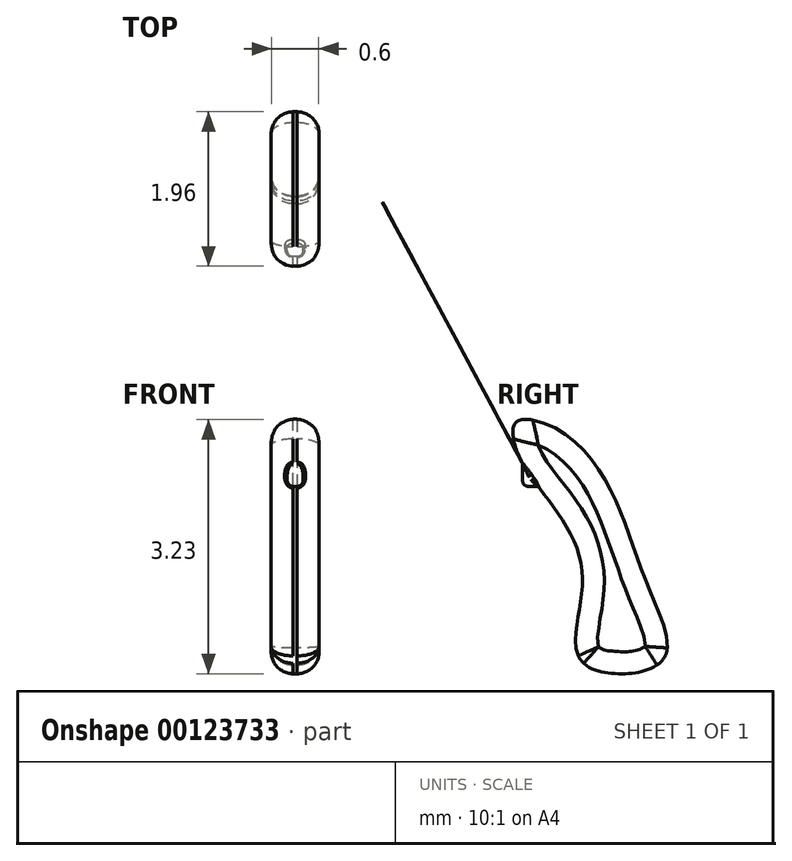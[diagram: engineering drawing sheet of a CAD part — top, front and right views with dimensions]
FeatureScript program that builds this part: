
annotation { "Feature Type Name" : "Feature", "Feature Type Description" : "" }
export const myFeature = defineFeature(function(context is Context, id is Id, definition is map)
    precondition{}
    {
        {
            var Q0;
            Q0=qCreatedBy(makeId("Right.planeOp"),FACE);
            var sketch = newSketch(context, id + "F0", { "sketchPlane" : qUnion([Q0])});
            skFitSpline(sketch, "E0", {"points": [v(0, 0) * mm, v(1, 0) * mm, v(0.83, 0.97) * mm, v(0, 2.7) * mm, v(-0.83, 3.06) * mm, v(-0.84, 2.71) * mm, v(-0.54, 2.2) * mm, v(0, 1.1) * mm, v(0, 0) * mm]});
            skSolve(sketch);
        }
        {
            var Q0;
            Q0=makeQuery(id+"F0.imprint","IMPRINT",FACE,{"disambiguationData":[TD([[makeQuery(id+"F0.imprint","IMPRINT",EDGE,{"derivedFrom":sQuery(id+"F0.wireOp",EDGE,"E0")}),1.0]])]});
            extrude(context, id + "F1", {"entities" : qUnion([Q0]), "depth" : 0.3 * mm});
        }
        {
            var Q0;
            Q0=makeQuery(id+"F0.imprint","IMPRINT",FACE,{"disambiguationData":[TD([[makeQuery(id+"F0.imprint","IMPRINT",EDGE,{"derivedFrom":sQuery(id+"F0.wireOp",EDGE,"E0")}),1.0]])]});
            extrude(context, id + "F2", {"entities" : qUnion([Q0]), "operationType" : NewBodyOperationType.ADD, "oppositeDirection" : true, "depth" : 0.3 * mm});
        }
        {
            var Q0;
            Q0=makeQuery(id+"F1.opExtrude","CAP_EDGE",EDGE,{"disambiguationData":[OSD([sQuery(id+"F0.wireOp",EDGE,"E0")])],"isStart":false});
            var Q1;
            Q1=makeQuery(id+"F2.opExtrude","CAP_EDGE",EDGE,{"disambiguationData":[OSD([sQuery(id+"F0.wireOp",EDGE,"E0")])],"isStart":false});
            fillet(context, id + "F3", {"entities" : qUnion([Q0, Q1]), "radius" : 0.28 * mm, "tangentPropagation" : true, "allowEdgeOverflow" : false});
        }
        {
            var Q0;
            Q0=qCreatedBy(makeId("Front.planeOp"),FACE);
            var sketch = newSketch(context, id + "F4", { "sketchPlane" : qUnion([Q0])});
            skLineSegment(sketch, "E1.bottom", {"start": v(0.1, 2.63) * mm, "end": v(-0.1, 2.63) * mm});
            skLineSegment(sketch, "E1.top", {"start": v(0.1, 2.23) * mm, "end": v(-0.1, 2.23) * mm});
            skLineSegment(sketch, "E1.left", {"start": v(0.1, 2.63) * mm, "end": v(0.1, 2.23) * mm});
            skLineSegment(sketch, "E1.right", {"start": v(-0.1, 2.63) * mm, "end": v(-0.1, 2.23) * mm});
            skPoint(sketch, "E1.middle", {"position": v(0, 2.43) * mm});
            skSolve(sketch);
        }
        {
            var Q0;
            Q0=makeQuery(id+"F4.imprint","IMPRINT",FACE,{"disambiguationData":[TD([[makeQuery(id+"F4.imprint","IMPRINT",EDGE,{"derivedFrom":sQuery(id+"F4.wireOp",EDGE,"E1.bottom")}),1.0]])]});
            extrude(context, id + "F5", {"entities" : qUnion([Q0]), "operationType" : NewBodyOperationType.ADD, "depth" : 0.76 * mm});
        }
        {
            var Q0;
            Q0=makeQuery(id+"F5.opExtrude","CAP_EDGE",EDGE,{"disambiguationData":[OSD([sQuery(id+"F4.wireOp",EDGE,"E1.left")])],"isStart":false});
            var Q1;
            Q1=makeQuery(id+"F5.opExtrude","SWEPT_EDGE",EDGE,{"disambiguationData":[OSD([sQuery(id+"F4.wireOp",EDGE,"E1.top"),sQuery(id+"F4.wireOp",EDGE,"E1.left")])]});
            var Q2;
            Q2=makeQuery(id+"F5.opExtrude","CAP_EDGE",EDGE,{"disambiguationData":[OSD([sQuery(id+"F4.wireOp",EDGE,"E1.right")])],"isStart":false});
            var Q3;
            Q3=makeQuery(id+"F5.opExtrude","SWEPT_EDGE",EDGE,{"disambiguationData":[OSD([sQuery(id+"F4.wireOp",EDGE,"E1.top"),sQuery(id+"F4.wireOp",EDGE,"E1.right")])]});
            fillet(context, id + "F6", {"entities" : qUnion([Q0, Q1, Q2, Q3]), "radius" : 0.08 * mm, "tangentPropagation" : true, "allowEdgeOverflow" : false});
        }
        {
            var Q0;
            Q0=makeQuery(id+"F5.opExtrude","CAP_EDGE",EDGE,{"disambiguationData":[OSD([sQuery(id+"F4.wireOp",EDGE,"E1.top")])],"isStart":false});
            fillet(context, id + "F7", {"entities" : qUnion([Q0]), "radius" : 0.08 * mm, "tangentPropagation" : true, "allowEdgeOverflow" : false});
        }
        {
            var Q0;
            {var subQ0=sQuery(id+"F0.wireOp",EDGE,"E0");Q0=makeQuery(id+"F5.boolean.opBoolean","INTERSECT",EDGE,{"derivedFrom":[makeQuery(id+"F3.opFillet","BLEND_FACE",FACE,{"disambiguationData":[OSD([subQ0]),TDD([makeQuery(id+"F2.opExtrude","CAP_EDGE",EDGE,{"disambiguationData":[OSD([subQ0])],"isStart":false})]),OD(3.0)]}),makeQuery(id+"F5.opExtrude","SWEPT_FACE",FACE,{"disambiguationData":[OSD([sQuery(id+"F4.wireOp",EDGE,"E1.right")])]})]});}
            fillet(context, id + "F8", {"entities" : qUnion([Q0]), "radius" : 0.05 * mm, "tangentPropagation" : true, "allowEdgeOverflow" : false});
        }
    });
